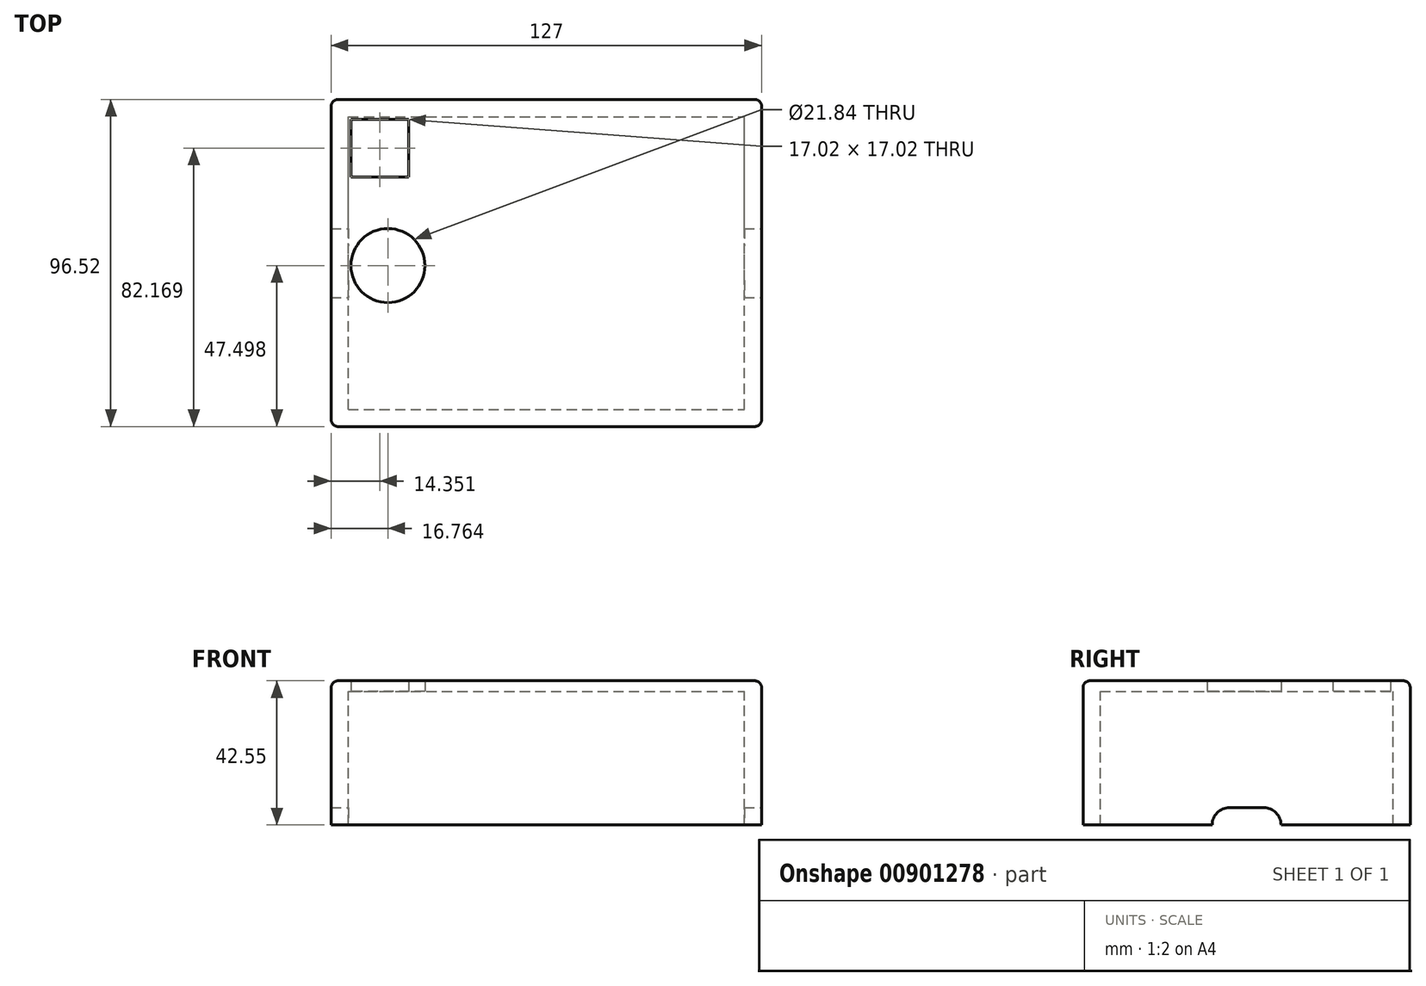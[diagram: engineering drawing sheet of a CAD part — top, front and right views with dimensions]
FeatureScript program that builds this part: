
annotation { "Feature Type Name" : "Feature", "Feature Type Description" : "" }
export const myFeature = defineFeature(function(context is Context, id is Id, definition is map)
    precondition{}
    {
        {
            var Q0;
            Q0=qCreatedBy(makeId("Top.planeOp"),FACE);
            var sketch = newSketch(context, id + "F0", { "sketchPlane" : qUnion([Q0])});
            skLineSegment(sketch, "E0.bottom", {"start": v(0, 0) * mm, "end": v(127, 0) * mm});
            skLineSegment(sketch, "E0.top", {"start": v(0, 96.52) * mm, "end": v(127, 96.52) * mm});
            skLineSegment(sketch, "E0.left", {"start": v(0, 0) * mm, "end": v(0, 96.52) * mm});
            skLineSegment(sketch, "E0.right", {"start": v(127, 0) * mm, "end": v(127, 96.52) * mm});
            skLineSegment(sketch, "E1.bottom", {"start": v(5.84, 90.68) * mm, "end": v(22.86, 90.68) * mm});
            skLineSegment(sketch, "E1.top", {"start": v(5.84, 73.66) * mm, "end": v(22.86, 73.66) * mm});
            skLineSegment(sketch, "E1.left", {"start": v(5.84, 90.68) * mm, "end": v(5.84, 73.66) * mm});
            skLineSegment(sketch, "E1.right", {"start": v(22.86, 90.68) * mm, "end": v(22.86, 73.66) * mm});
            skCircle(sketch, "E2", {"center": v(16.76, 47.5) * mm, "radius": 10.92 * mm});
            skSolve(sketch);
        }
        {
            var Q0;
            Q0 = qSketchRegion(id + "F0", true);
            extrude(context, id + "F1", {"entities" : qUnion([Q0]), "depth" : 3.17 * mm, "offsetDistance" : 25.4 * mm});
        }
        {
            var Q0;
            Q0=makeQuery(id+"F1.opExtrude","CAP_FACE",FACE,{"disambiguationData":[OSD([sQuery(id+"F0.wireOp",EDGE,"E0.bottom"),sQuery(id+"F0.wireOp",EDGE,"E0.top"),sQuery(id+"F0.wireOp",EDGE,"E0.left"),sQuery(id+"F0.wireOp",EDGE,"E0.right"),sQuery(id+"F0.wireOp",EDGE,"E1.bottom"),sQuery(id+"F0.wireOp",EDGE,"E1.top"),sQuery(id+"F0.wireOp",EDGE,"E1.left"),sQuery(id+"F0.wireOp",EDGE,"E1.right"),sQuery(id+"F0.wireOp",EDGE,"E2")])],"isStart":true});
            var sketch = newSketch(context, id + "F2", { "sketchPlane" : qUnion([Q0])});
            skLineSegment(sketch, "E3.bottom", {"start": v(0, 0) * mm, "end": v(127, 0) * mm});
            skLineSegment(sketch, "E3.top", {"start": v(0, -96.52) * mm, "end": v(127, -96.52) * mm});
            skLineSegment(sketch, "E3.left", {"start": v(0, 0) * mm, "end": v(0, -96.52) * mm});
            skLineSegment(sketch, "E3.right", {"start": v(127, 0) * mm, "end": v(127, -96.52) * mm});
            skLineSegment(sketch, "E4.0", {"start": v(5.08, -5.08) * mm, "end": v(121.92, -5.08) * mm});
            skLineSegment(sketch, "E4.1", {"start": v(5.08, -5.08) * mm, "end": v(5.08, -91.44) * mm});
            skLineSegment(sketch, "E4.2", {"start": v(5.08, -91.44) * mm, "end": v(121.92, -91.44) * mm});
            skLineSegment(sketch, "E4.3", {"start": v(121.92, -5.08) * mm, "end": v(121.92, -91.44) * mm});
            skSolve(sketch);
        }
        {
            var Q0;
            Q0 = qSketchRegion(id + "F2", true);
            extrude(context, id + "F3", {"entities" : qUnion([Q0]), "operationType" : NewBodyOperationType.ADD, "depth" : 39.37 * mm, "offsetDistance" : 25.4 * mm});
        }
        {
            var Q0;
            Q0=makeQuery(id+"F3.boolean.opBoolean","MERGE",EDGE,{"derivedFrom":[makeQuery(id+"F1.opExtrude","SWEPT_EDGE",EDGE,{"disambiguationData":[OSD([sQuery(id+"F0.wireOp",EDGE,"E0.top"),sQuery(id+"F0.wireOp",EDGE,"E0.left")])]}),makeQuery(id+"F3.opExtrude","SWEPT_EDGE",EDGE,{"disambiguationData":[OSD([sQuery(id+"F2.wireOp",EDGE,"E3.top"),sQuery(id+"F2.wireOp",EDGE,"E3.left")])]})]});
            var Q1;
            Q1=makeQuery(id+"F1.opExtrude","CAP_EDGE",EDGE,{"disambiguationData":[OSD([sQuery(id+"F0.wireOp",EDGE,"E0.top")])],"isStart":false});
            var Q2;
            Q2=makeQuery(id+"F1.opExtrude","CAP_EDGE",EDGE,{"disambiguationData":[OSD([sQuery(id+"F0.wireOp",EDGE,"E0.left")])],"isStart":false});
            var Q3;
            Q3=makeQuery(id+"F3.boolean.opBoolean","MERGE",EDGE,{"derivedFrom":[makeQuery(id+"F1.opExtrude","SWEPT_EDGE",EDGE,{"disambiguationData":[OSD([sQuery(id+"F0.wireOp",EDGE,"E0.top"),sQuery(id+"F0.wireOp",EDGE,"E0.right")])]}),makeQuery(id+"F3.opExtrude","SWEPT_EDGE",EDGE,{"disambiguationData":[OSD([sQuery(id+"F2.wireOp",EDGE,"E3.top"),sQuery(id+"F2.wireOp",EDGE,"E3.right")])]})]});
            var Q4;
            Q4=makeQuery(id+"F1.opExtrude","CAP_EDGE",EDGE,{"disambiguationData":[OSD([sQuery(id+"F0.wireOp",EDGE,"E0.right")])],"isStart":false});
            var Q5;
            Q5=makeQuery(id+"F3.boolean.opBoolean","MERGE",EDGE,{"derivedFrom":[makeQuery(id+"F1.opExtrude","SWEPT_EDGE",EDGE,{"disambiguationData":[OSD([sQuery(id+"F0.wireOp",EDGE,"E0.bottom"),sQuery(id+"F0.wireOp",EDGE,"E0.right")])]}),makeQuery(id+"F3.opExtrude","SWEPT_EDGE",EDGE,{"disambiguationData":[OSD([sQuery(id+"F2.wireOp",EDGE,"E3.bottom"),sQuery(id+"F2.wireOp",EDGE,"E3.right")])]})]});
            var Q6;
            Q6=makeQuery(id+"F1.opExtrude","CAP_EDGE",EDGE,{"disambiguationData":[OSD([sQuery(id+"F0.wireOp",EDGE,"E0.bottom")])],"isStart":false});
            var Q7;
            Q7=makeQuery(id+"F3.boolean.opBoolean","MERGE",EDGE,{"derivedFrom":[makeQuery(id+"F1.opExtrude","SWEPT_EDGE",EDGE,{"disambiguationData":[OSD([sQuery(id+"F0.wireOp",EDGE,"E0.bottom"),sQuery(id+"F0.wireOp",EDGE,"E0.left")])]}),makeQuery(id+"F3.opExtrude","SWEPT_EDGE",EDGE,{"disambiguationData":[OSD([sQuery(id+"F2.wireOp",EDGE,"E3.bottom"),sQuery(id+"F2.wireOp",EDGE,"E3.left")])]})]});
            fillet(context, id + "F4", {"entities" : qUnion([Q0, Q1, Q2, Q3, Q4, Q5, Q6, Q7]), "radius" : 2.03 * mm, "tangentPropagation" : true, "allowEdgeOverflow" : false});
        }
        {
            var Q0;
            Q0=makeQuery(id+"F3.opExtrude","CAP_FACE",FACE,{"disambiguationData":[OSD([sQuery(id+"F2.wireOp",EDGE,"E3.bottom"),sQuery(id+"F2.wireOp",EDGE,"E3.top"),sQuery(id+"F2.wireOp",EDGE,"E3.left"),sQuery(id+"F2.wireOp",EDGE,"E3.right"),sQuery(id+"F2.wireOp",EDGE,"E4.0"),sQuery(id+"F2.wireOp",EDGE,"E4.1"),sQuery(id+"F2.wireOp",EDGE,"E4.2"),sQuery(id+"F2.wireOp",EDGE,"E4.3")])],"isStart":false});
            var sketch = newSketch(context, id + "F5", { "sketchPlane" : qUnion([Q0])});
            skLineSegment(sketch, "E5.bottom", {"start": v(121.92, -38.1) * mm, "end": v(127, -38.1) * mm});
            skLineSegment(sketch, "E5.top", {"start": v(121.92, -58.42) * mm, "end": v(127, -58.42) * mm});
            skLineSegment(sketch, "E5.left", {"start": v(121.92, -38.1) * mm, "end": v(121.92, -58.42) * mm});
            skLineSegment(sketch, "E5.right", {"start": v(127, -38.1) * mm, "end": v(127, -58.42) * mm});
            skLineSegment(sketch, "E6.bottom", {"start": v(0, -38.1) * mm, "end": v(5.08, -38.1) * mm});
            skLineSegment(sketch, "E6.top", {"start": v(0, -58.42) * mm, "end": v(5.08, -58.42) * mm});
            skLineSegment(sketch, "E6.left", {"start": v(0, -38.1) * mm, "end": v(0, -58.42) * mm});
            skLineSegment(sketch, "E6.right", {"start": v(5.08, -38.1) * mm, "end": v(5.08, -58.42) * mm});
            skSolve(sketch);
        }
        {
            var Q0;
            Q0 = qSketchRegion(id + "F5", true);
            extrude(context, id + "F6", {"entities" : qUnion([Q0]), "operationType" : NewBodyOperationType.REMOVE, "oppositeDirection" : true, "depth" : 5.08 * mm, "offsetDistance" : 25.4 * mm});
        }
        {
            var Q0;
            Q0=makeQuery(id+"F6.boolean.opBoolean","COPY",EDGE,{"derivedFrom":makeQuery(id+"F6.opExtrude","CAP_EDGE",EDGE,{"disambiguationData":[OSD([sQuery(id+"F5.wireOp",EDGE,"E6.bottom")])],"isStart":false})});
            var Q1;
            Q1=makeQuery(id+"F6.boolean.opBoolean","COPY",EDGE,{"derivedFrom":makeQuery(id+"F6.opExtrude","CAP_EDGE",EDGE,{"disambiguationData":[OSD([sQuery(id+"F5.wireOp",EDGE,"E6.top")])],"isStart":false})});
            var Q2;
            Q2=makeQuery(id+"F6.boolean.opBoolean","COPY",EDGE,{"derivedFrom":makeQuery(id+"F6.opExtrude","CAP_EDGE",EDGE,{"disambiguationData":[OSD([sQuery(id+"F5.wireOp",EDGE,"E5.top")])],"isStart":false})});
            var Q3;
            Q3=makeQuery(id+"F6.boolean.opBoolean","COPY",EDGE,{"derivedFrom":makeQuery(id+"F6.opExtrude","CAP_EDGE",EDGE,{"disambiguationData":[OSD([sQuery(id+"F5.wireOp",EDGE,"E5.bottom")])],"isStart":false})});
            fillet(context, id + "F7", {"entities" : qUnion([Q0, Q1, Q2, Q3]), "radius" : 5.08 * mm, "tangentPropagation" : true, "allowEdgeOverflow" : false});
        }
    });
